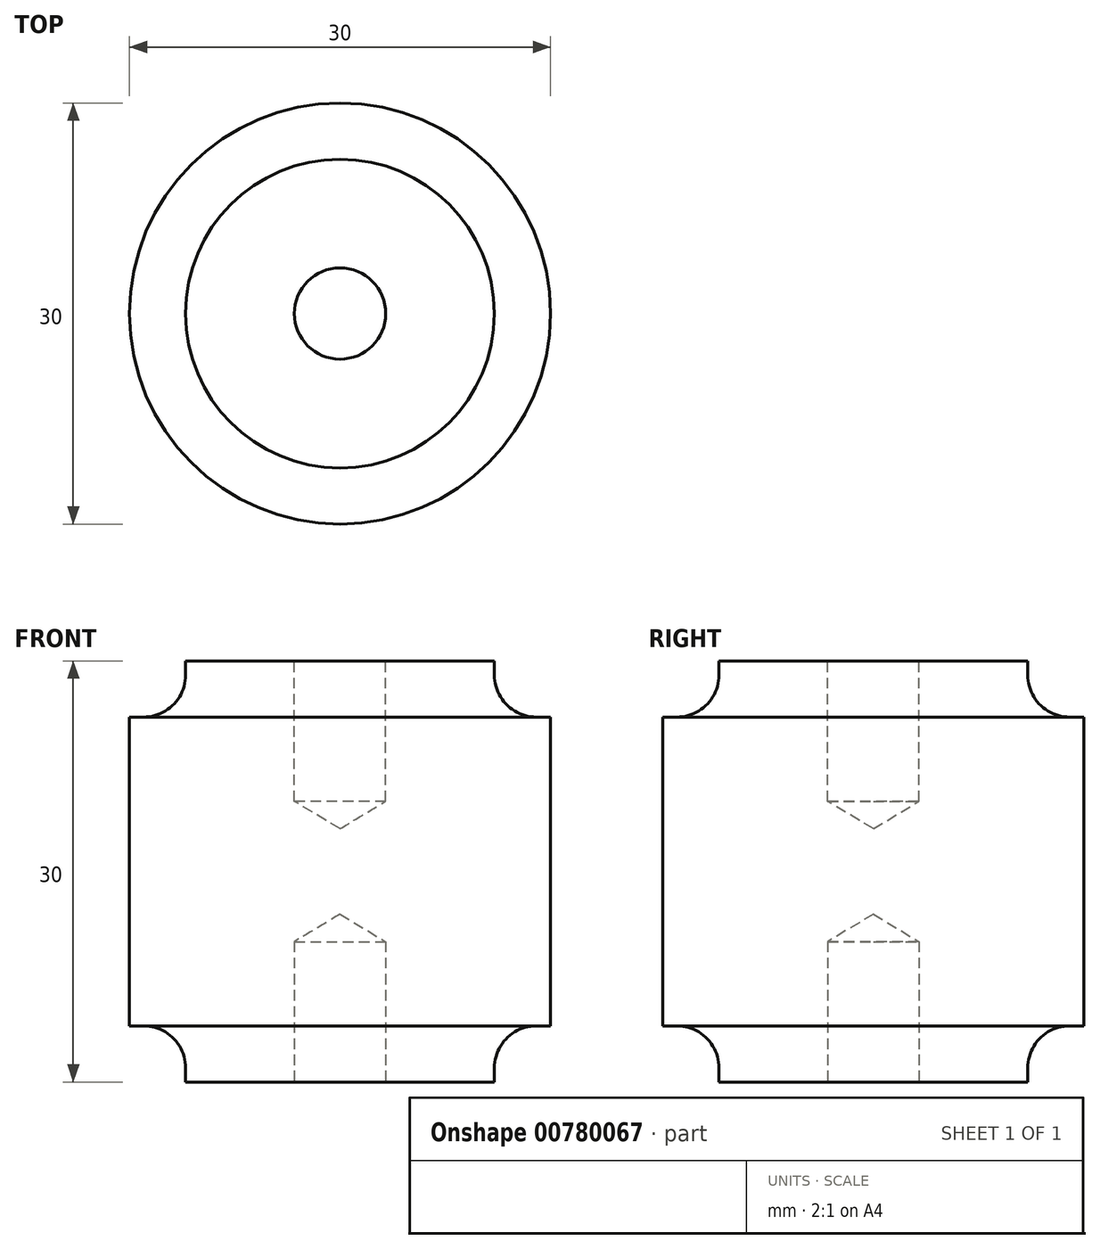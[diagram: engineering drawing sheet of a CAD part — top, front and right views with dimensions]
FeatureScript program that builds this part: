
annotation { "Feature Type Name" : "Feature", "Feature Type Description" : "" }
export const myFeature = defineFeature(function(context is Context, id is Id, definition is map)
    precondition{}
    {
        {
            var Q0;
            Q0=qCreatedBy(makeId("Front.planeOp"),FACE);
            var sketch = newSketch(context, id + "F0", { "sketchPlane" : qUnion([Q0])});
            skPoint(sketch, "E0.middle", {"position": v(0, 0) * mm});
            skLineSegment(sketch, "E1.0", {"start": v(0, 15) * mm, "end": v(-11, 15) * mm});
            skLineSegment(sketch, "E1.2", {"start": v(0, -15) * mm, "end": v(-11, -15) * mm});
            skLineSegment(sketch, "E1.3", {"start": v(-15, 11) * mm, "end": v(-15, -11) * mm});
            skLineSegment(sketch, "E2.bottom", {"start": v(-11, 11) * mm, "end": v(-15, 11) * mm});
            skLineSegment(sketch, "E2.left", {"start": v(-11, 11) * mm, "end": v(-11, 15) * mm});
            skLineSegment(sketch, "E3.bottom", {"start": v(-11, -11) * mm, "end": v(-15, -11) * mm});
            skLineSegment(sketch, "E3.left", {"start": v(-11, -11) * mm, "end": v(-11, -15) * mm});
            skLineSegment(sketch, "E4.left", {"start": v(0, 15) * mm, "end": v(0, -15) * mm});
            skSolve(sketch);
        }
        {
            var Q0;
            Q0=makeQuery(id+"F0.imprint","IMPRINT",FACE,{"disambiguationData":[TD([[makeQuery(id+"F0.imprint","IMPRINT",EDGE,{"derivedFrom":sQuery(id+"F0.wireOp",EDGE,"E1.0")}),1.0]])]});
            var Q1;
            Q1=sQuery(id+"F0.wireOp",EDGE,"E4.left");
            revolve(context, id + "F1", {"entities" : qUnion([Q0]), "axis" : qUnion([Q1]), "revolveType" : RevolveType.FULL});
        }
        {
            var Q0;
            Q0=makeQuery(id+"F1.opRevolve","SWEPT_EDGE",EDGE,{"disambiguationData":[OSD([sQuery(id+"F0.wireOp",EDGE,"E2.bottom"),sQuery(id+"F0.wireOp",EDGE,"E2.left")])]});
            var Q1;
            Q1=makeQuery(id+"F1.opRevolve","SWEPT_EDGE",EDGE,{"disambiguationData":[OSD([sQuery(id+"F0.wireOp",EDGE,"E3.bottom"),sQuery(id+"F0.wireOp",EDGE,"E3.left")])]});
            fillet(context, id + "F2", {"entities" : qUnion([Q0, Q1]), "radius" : 3 * mm, "tangentPropagation" : true, "allowEdgeOverflow" : false});
        }
        {
            var Q0;
            Q0=makeQuery(id+"F1.opRevolve","SWEPT_FACE",FACE,{"disambiguationData":[OSD([sQuery(id+"F0.wireOp",EDGE,"E1.0")])]});
            var sketch = newSketch(context, id + "F3", { "sketchPlane" : qUnion([Q0])});
            skPoint(sketch, "E5", {"position": v(0, 0) * mm});
            skSolve(sketch);
        }
        {
            var Q0;
            Q0=makeQuery(id+"F1.opRevolve","SWEPT_FACE",FACE,{"disambiguationData":[OSD([sQuery(id+"F0.wireOp",EDGE,"E1.2")])]});
            var sketch = newSketch(context, id + "F4", { "sketchPlane" : qUnion([Q0])});
            skPoint(sketch, "E6", {"position": v(0, 0) * mm});
            skSolve(sketch);
        }
        {
            var Q0;
            Q0=sQuery(id+"F4.wireOp",VERTEX,"E6");
            var Q1;
            Q1=sQuery(id+"F3.wireOp",VERTEX,"E5");
            var Q2;
            Q2=makeQuery(id+"F1.opRevolve","SWEPT_BODY",BODY,{"disambiguationData":[OSD([sQuery(id+"F0.wireOp",EDGE,"E1.0"),sQuery(id+"F0.wireOp",EDGE,"E1.2"),sQuery(id+"F0.wireOp",EDGE,"E1.3"),sQuery(id+"F0.wireOp",EDGE,"E2.bottom"),sQuery(id+"F0.wireOp",EDGE,"E2.left"),sQuery(id+"F0.wireOp",EDGE,"E3.bottom"),sQuery(id+"F0.wireOp",EDGE,"E3.left"),sQuery(id+"F0.wireOp",EDGE,"E4.left")])]});
            hole(context, id + "F5", {"style" : HoleStyle.SIMPLE, "endStyle" : HoleEndStyle.BLIND, "holeDiameter" : 6.5 * mm, "holeDepth" : 10 * mm, "locations" : qUnion([Q0, Q1]), "scope" : qUnion([Q2]), "majorDiameter" : 5 * mm, "tappedDepth" : 12 * mm, "tapClearance" : 3});
        }
    });
